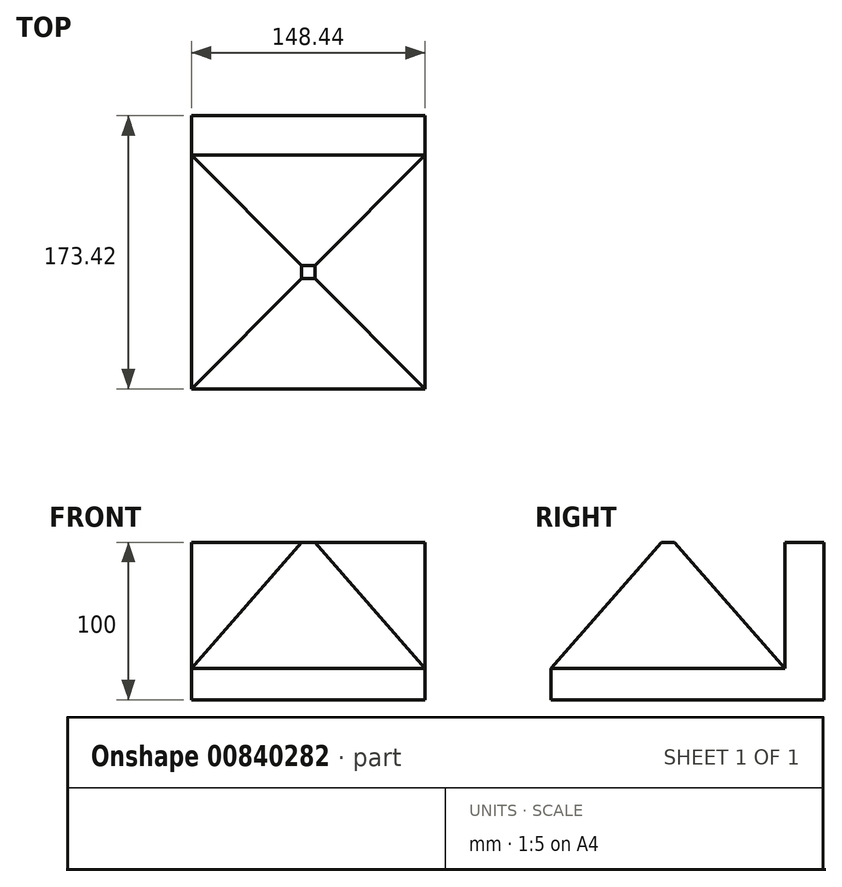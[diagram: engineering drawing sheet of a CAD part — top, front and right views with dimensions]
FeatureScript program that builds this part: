
annotation { "Feature Type Name" : "Feature", "Feature Type Description" : "" }
export const myFeature = defineFeature(function(context is Context, id is Id, definition is map)
    precondition{}
    {
        {
            var Q0;
            Q0=qCreatedBy(makeId("Top.planeOp"),FACE);
            var sketch = newSketch(context, id + "F0", { "sketchPlane" : qUnion([Q0])});
            skLineSegment(sketch, "E0.bottom", {"start": v(74.23, 73.98) * mm, "end": v(-74.2, 73.98) * mm});
            skLineSegment(sketch, "E0.top", {"start": v(74.23, -74.44) * mm, "end": v(-74.2, -74.44) * mm});
            skLineSegment(sketch, "E0.left", {"start": v(74.23, 73.98) * mm, "end": v(74.23, -74.44) * mm});
            skLineSegment(sketch, "E0.right", {"start": v(-74.2, 73.98) * mm, "end": v(-74.2, -74.44) * mm});
            skSolve(sketch);
        }
        {
            var Q0;
            Q0=makeQuery(id+"F0.imprint","IMPRINT",FACE,{"disambiguationData":[TD([[makeQuery(id+"F0.imprint","IMPRINT",EDGE,{"derivedFrom":sQuery(id+"F0.wireOp",EDGE,"E0.bottom")}),1.0]])]});
            extrude(context, id + "F1", {"entities" : qUnion([Q0]), "depth" : 100 * mm, "offsetDistance" : 25 * mm});
        }
        {
            var Q0;
            Q0=makeQuery(id+"F1.opExtrude","CAP_FACE",FACE,{"disambiguationData":[OSD([sQuery(id+"F0.wireOp",EDGE,"E0.bottom"),sQuery(id+"F0.wireOp",EDGE,"E0.top"),sQuery(id+"F0.wireOp",EDGE,"E0.left"),sQuery(id+"F0.wireOp",EDGE,"E0.right")])],"isStart":false});
            chamfer(context, id + "F2", {"entities" : qUnion([Q0]), "chamferType" : ChamferType.TWO_OFFSETS, "width1" : 70 * mm, "oppositeDirection" : false, "width2" : 80 * mm, "tangentPropagation" : true});
        }
        {
            var Q0;
            Q0=makeQuery(id+"F1.opExtrude","SWEPT_FACE",FACE,{"disambiguationData":[OSD([sQuery(id+"F0.wireOp",EDGE,"E0.bottom")])]});
            extrude(context, id + "F3", {"entities" : qUnion([Q0]), "operationType" : NewBodyOperationType.ADD, "depth" : 25 * mm, "offsetDistance" : 25 * mm});
        }
        {
            var Q0;
            {var subQ0=sQuery(id+"F0.wireOp",EDGE,"E0.bottom");Q0=makeQuery(id+"F3.opExtrude","SWEPT_FACE",FACE,{"disambiguationData":[OSD([subQ0]),TDD([makeQuery(id+"F2.opChamfer","BLEND_EDGE",EDGE,{"blendedFrom":[makeQuery(id+"F1.opExtrude","CAP_EDGE",EDGE,{"disambiguationData":[OSD([subQ0])],"isStart":false}),makeQuery(id+"F1.opExtrude","SWEPT_FACE",FACE,{"disambiguationData":[OSD([subQ0])]})],"blendedInto":[makeQuery(id+"F1.opExtrude","SWEPT_FACE",FACE,{"disambiguationData":[OSD([subQ0])]})]})])]});}
            extrude(context, id + "F4", {"entities" : qUnion([Q0]), "operationType" : NewBodyOperationType.ADD, "depth" : 80 * mm, "offsetDistance" : 25 * mm});
        }
    });
